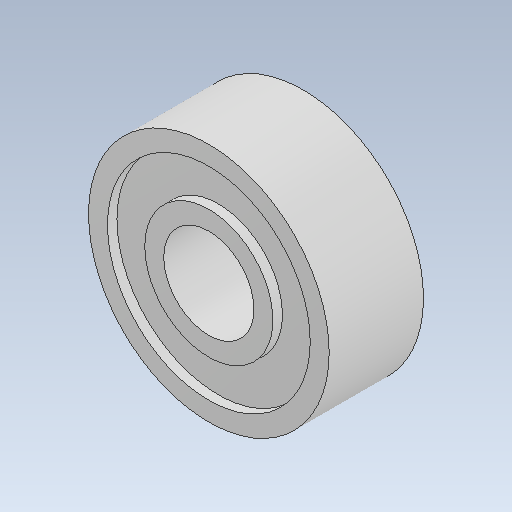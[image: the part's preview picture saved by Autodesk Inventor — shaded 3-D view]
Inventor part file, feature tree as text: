
AUTODESK INVENTOR PART (.ipt)
format: ipt  version: 2020 (Build 240168000, 168)  size: 118,784 bytes
history: native  units: in
note: dims shown in document units (in); Inventor stores cm internally (conversion verified against a paired STEP export)
features: revolve x1
ambient origin geometry x8: Origin, YZ Plane, XZ Plane, XY Plane, X Axis, Y Axis, Z Axis, Center Point
bodies: Solid1 (feature_tree)
feature tree (1):
  revolve  "Revolve1"  [1 undecoded]
note: 1 required parameter value undecoded (feature->parameter linkage not recoverable at this tier; creation-order binding heuristic only, values carry confidence <= 0.55)
